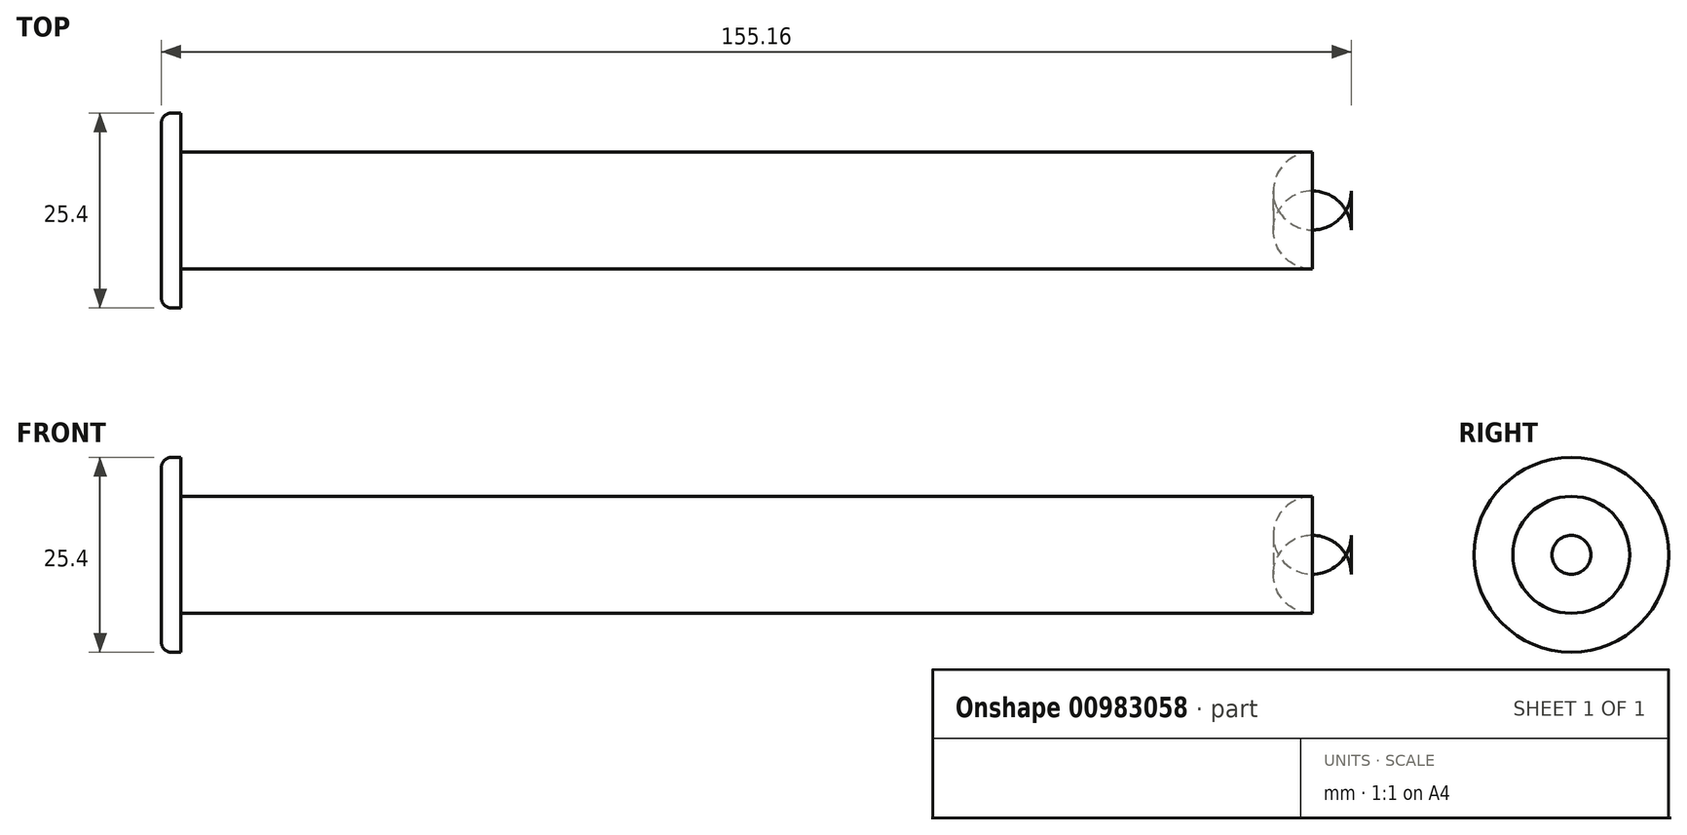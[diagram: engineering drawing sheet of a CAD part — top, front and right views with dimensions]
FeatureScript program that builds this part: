
annotation { "Feature Type Name" : "Feature", "Feature Type Description" : "" }
export const myFeature = defineFeature(function(context is Context, id is Id, definition is map)
    precondition{}
    {
        {
            var Q0;
            Q0=qCreatedBy(makeId("Top.planeOp"),FACE);
            var sketch = newSketch(context, id + "F0", { "sketchPlane" : qUnion([Q0])});
            skLineSegment(sketch, "E0", {"start": v(-96.64, 0) * mm, "end": v(55.98, 0) * mm});
            skLineSegment(sketch, "E1", {"start": v(55.98, 0) * mm, "end": v(55.98, 7.62) * mm});
            skLineSegment(sketch, "E2", {"start": v(55.98, 7.62) * mm, "end": v(-96.64, 7.62) * mm});
            skLineSegment(sketch, "E3", {"start": v(-96.64, 7.62) * mm, "end": v(-96.64, 0) * mm});
            skSolve(sketch);
        }
        {
            var Q0;
            Q0=makeQuery(id+"F0.imprint","IMPRINT",FACE,{"disambiguationData":[TD([[makeQuery(id+"F0.imprint","IMPRINT",EDGE,{"derivedFrom":sQuery(id+"F0.wireOp",EDGE,"E0")}),1.0]])]});
            var Q1;
            Q1=sQuery(id+"F0.wireOp",EDGE,"E0");
            revolve(context, id + "F1", {"surfaceOperationType" : NewSurfaceOperationType.NEW, "entities" : qUnion([Q0]), "axis" : qUnion([Q1]), "revolveType" : RevolveType.FULL});
        }
        {
            var Q0;
            Q0=makeQuery(id+"F1.opRevolve","SWEPT_EDGE",EDGE,{"disambiguationData":[OSD([sQuery(id+"F0.wireOp",EDGE,"E1"),sQuery(id+"F0.wireOp",EDGE,"E2")])]});
            fillet(context, id + "F2", {"entities" : qUnion([Q0]), "radius" : 5.08 * mm, "tangentPropagation" : true, "allowEdgeOverflow" : false});
        }
        {
            var Q0;
            Q0=makeQuery(id+"F1.opRevolve","SWEPT_FACE",FACE,{"disambiguationData":[OSD([sQuery(id+"F0.wireOp",EDGE,"E3")])]});
            var sketch = newSketch(context, id + "F3", { "sketchPlane" : qUnion([Q0])});
            skCircle(sketch, "E4", {"center": v(0, 0) * mm, "radius": 12.7 * mm});
            skSolve(sketch);
        }
        {
            var Q0;
            Q0=qSketchRegion(id+"F3",true);
            extrude(context, id + "F4", {"entities" : qUnion([Q0]), "operationType" : NewBodyOperationType.ADD, "depth" : 2.54 * mm, "offsetDistance" : 25.4 * mm});
        }
        {
            var Q0;
            Q0=makeQuery(id+"F4.opExtrude","CAP_EDGE",EDGE,{"disambiguationData":[OSD([sQuery(id+"F3.wireOp",EDGE,"E4")])],"isStart":false});
            var Q1;
            Q1=makeQuery(id+"F1.opRevolve","SWEPT_EDGE",EDGE,{"disambiguationData":[OSD([sQuery(id+"F0.wireOp",EDGE,"E2"),sQuery(id+"F0.wireOp",EDGE,"E3")])]});
            fillet(context, id + "F5", {"entities" : qUnion([Q0, Q1]), "radius" : 1.27 * mm, "tangentPropagation" : true, "allowEdgeOverflow" : false});
        }
    });
